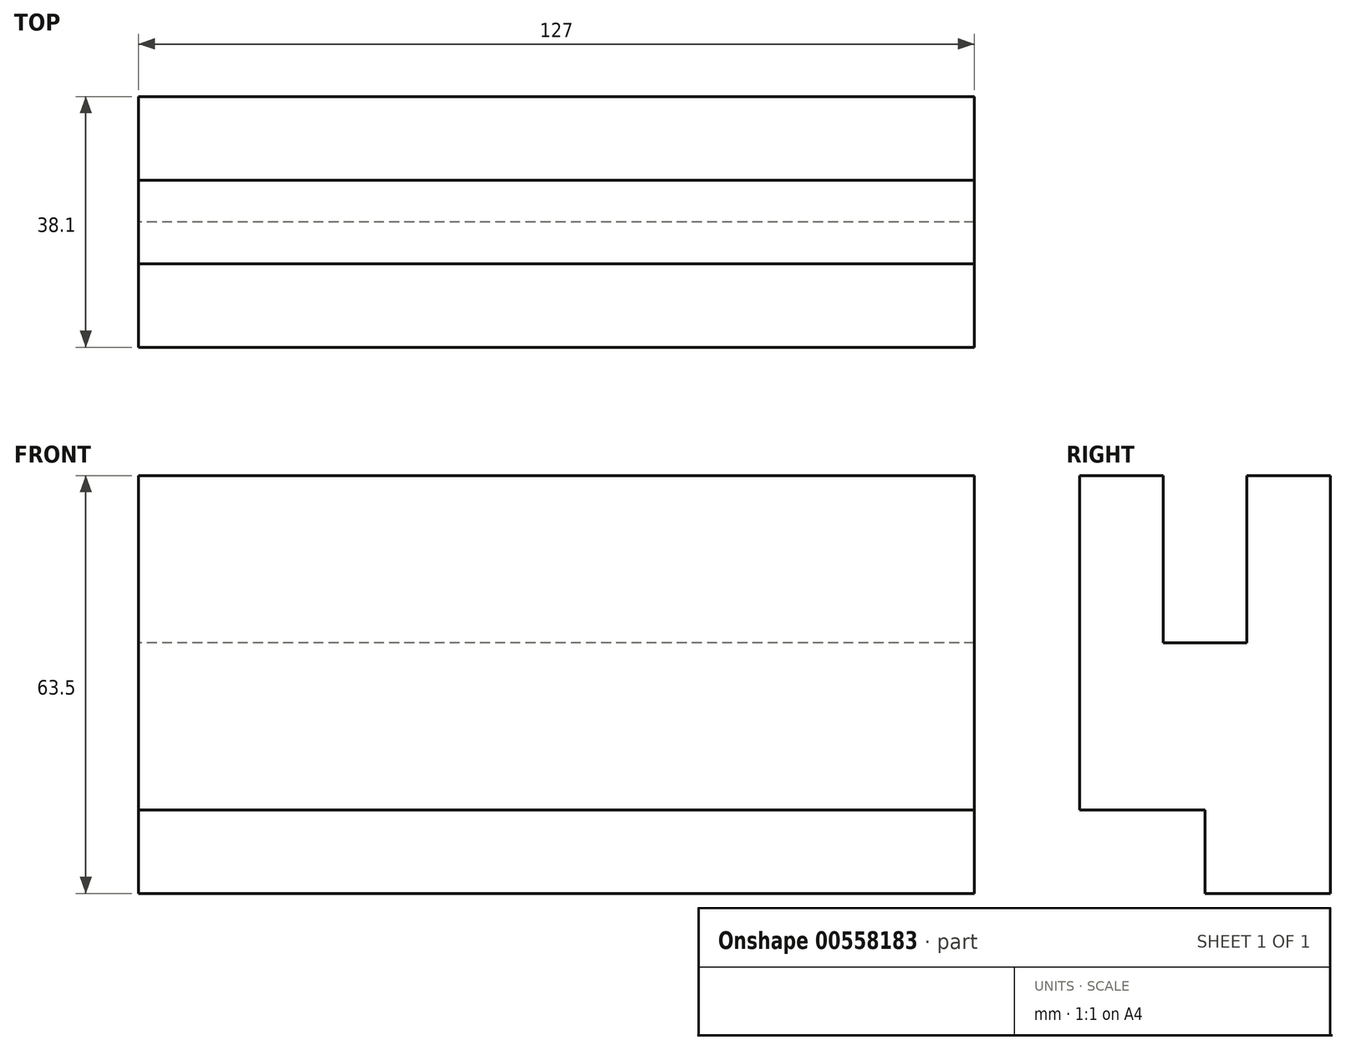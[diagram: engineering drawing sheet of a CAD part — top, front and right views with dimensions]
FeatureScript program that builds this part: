
annotation { "Feature Type Name" : "Feature", "Feature Type Description" : "" }
export const myFeature = defineFeature(function(context is Context, id is Id, definition is map)
    precondition{}
    {
        {
            var Q0;
            Q0=qCreatedBy(makeId("Right.planeOp"),FACE);
            var sketch = newSketch(context, id + "F0", { "sketchPlane" : qUnion([Q0])});
            skLineSegment(sketch, "E0", {"start": v(-38.1, 63.5) * mm, "end": v(-25.4, 63.5) * mm});
            skLineSegment(sketch, "E1", {"start": v(-25.4, 63.5) * mm, "end": v(-25.4, 38.1) * mm});
            skLineSegment(sketch, "E2", {"start": v(-25.4, 38.1) * mm, "end": v(-12.7, 38.1) * mm});
            skLineSegment(sketch, "E3", {"start": v(-12.7, 38.1) * mm, "end": v(-12.7, 63.5) * mm});
            skLineSegment(sketch, "E4", {"start": v(-12.7, 63.5) * mm, "end": v(0, 63.5) * mm});
            skLineSegment(sketch, "E5", {"start": v(0, 63.5) * mm, "end": v(0, 0) * mm});
            skLineSegment(sketch, "E6", {"start": v(0, 0) * mm, "end": v(-19.05, 0) * mm});
            skLineSegment(sketch, "E7", {"start": v(-19.05, 0) * mm, "end": v(-19.05, 12.7) * mm});
            skLineSegment(sketch, "E8", {"start": v(-19.05, 12.7) * mm, "end": v(-38.1, 12.7) * mm});
            skLineSegment(sketch, "E9", {"start": v(-38.1, 12.7) * mm, "end": v(-38.1, 63.5) * mm});
            skSolve(sketch);
        }
        {
            var Q0;
            Q0=makeQuery(id+"F0.imprint","IMPRINT",FACE,{"disambiguationData":[TD([[makeQuery(id+"F0.imprint","IMPRINT",EDGE,{"derivedFrom":sQuery(id+"F0.wireOp",EDGE,"E0")}),-1.0]])]});
            extrude(context, id + "F1", {"entities" : qUnion([Q0]), "depth" : 127 * mm, "offsetDistance" : 25.4 * mm});
        }
    });
